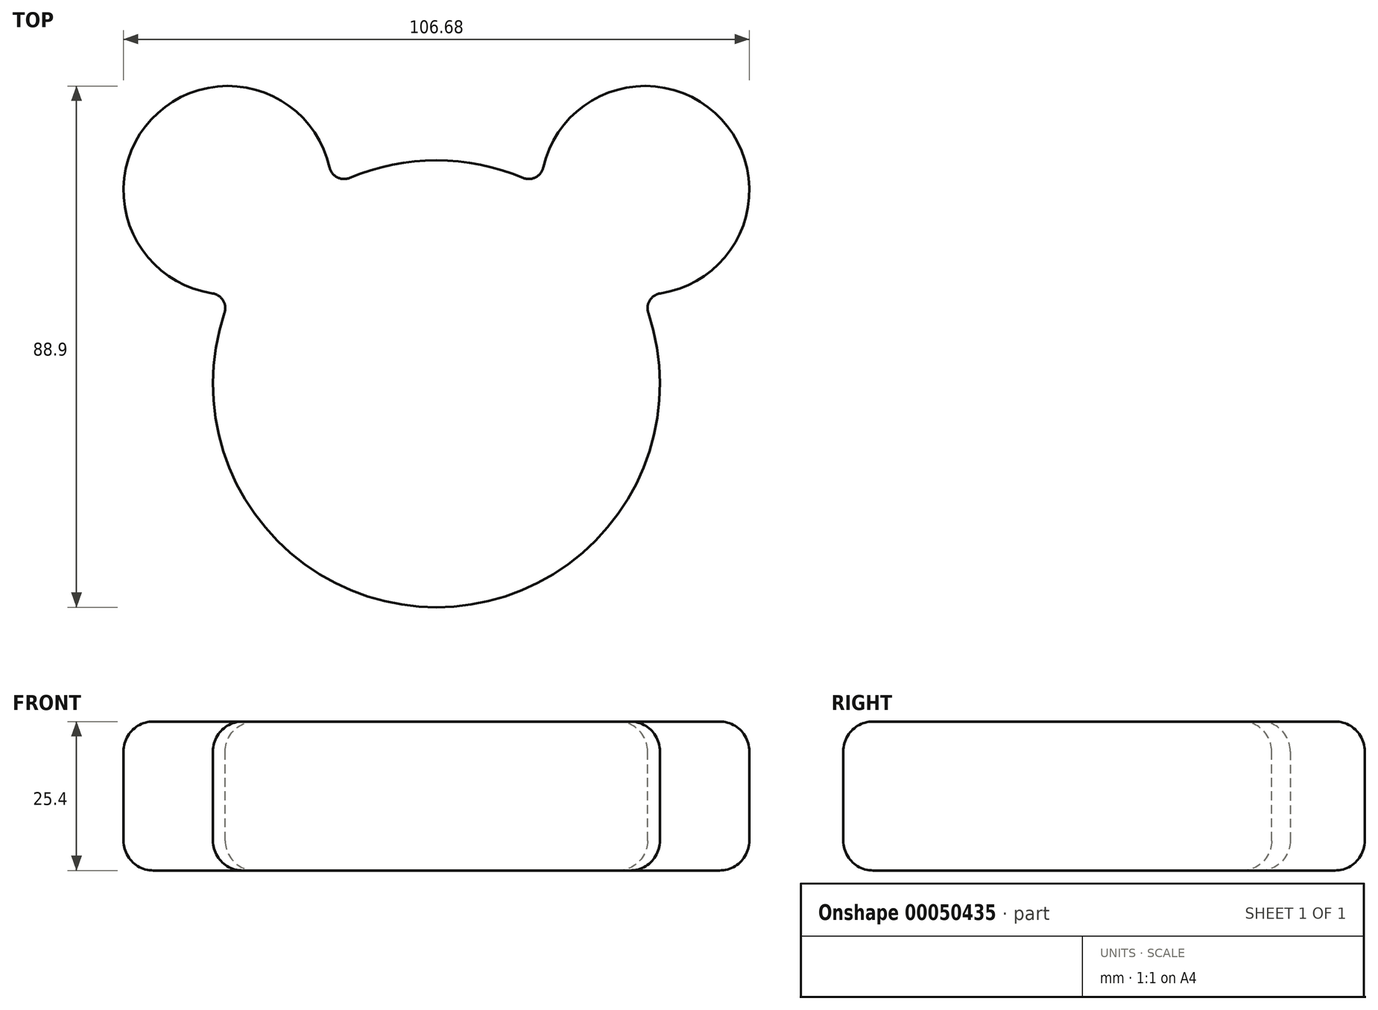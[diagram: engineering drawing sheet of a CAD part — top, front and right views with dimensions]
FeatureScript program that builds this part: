
annotation { "Feature Type Name" : "Feature", "Feature Type Description" : "" }
export const myFeature = defineFeature(function(context is Context, id is Id, definition is map)
    precondition{}
    {
        {
            var Q0;
            Q0=qCreatedBy(makeId("Top.planeOp"),FACE);
            var sketch = newSketch(context, id + "F0", { "sketchPlane" : qUnion([Q0])});
            skArc(sketch, "E0", {"start": v(-34.91, 15.25) * mm, "mid": v(0, -38.1) * mm, "end": v(34.91, 15.25) * mm});
            skArc(sketch, "E1", {"start": v(-17.8, 33.7) * mm, "mid": v(-48.59, 45.12) * mm, "end": v(-34.91, 15.25) * mm});
            skArc(sketch, "E2", {"start": v(34.91, 15.25) * mm, "mid": v(48.59, 45.12) * mm, "end": v(17.8, 33.7) * mm});
            skLineSegment(sketch, "E3", {"start": v(-35.56, 33.02) * mm, "end": v(0, 33.02) * mm, "construction": true});
            skLineSegment(sketch, "E4", {"start": v(0, 33.02) * mm, "end": v(35.56, 33.02) * mm, "construction": true});
            skArc(sketch, "E5.trimOffspring", {"start": v(17.8, 33.7) * mm, "mid": v(0, 38.1) * mm, "end": v(-17.8, 33.7) * mm});
            skSolve(sketch);
        }
        {
            var Q0;
            Q0=makeQuery(id+"F0.imprint","IMPRINT",FACE,{"disambiguationData":[TD([[makeQuery(id+"F0.imprint","IMPRINT",EDGE,{"derivedFrom":sQuery(id+"F0.wireOp",EDGE,"E0")}),1.0]])]});
            extrude(context, id + "F1", {"entities" : qUnion([Q0]), "depth" : 25.4 * mm});
        }
        {
            var Q0;
            Q0=makeQuery(id+"F1.opExtrude","SWEPT_EDGE",EDGE,{"disambiguationData":[OSD([sQuery(id+"F0.wireOp",EDGE,"E0"),sQuery(id+"F0.wireOp",EDGE,"E1")])]});
            var Q1;
            Q1=makeQuery(id+"F1.opExtrude","SWEPT_EDGE",EDGE,{"disambiguationData":[OSD([sQuery(id+"F0.wireOp",EDGE,"E1"),sQuery(id+"F0.wireOp",EDGE,"E5.trimOffspring")])]});
            var Q2;
            Q2=makeQuery(id+"F1.opExtrude","SWEPT_EDGE",EDGE,{"disambiguationData":[OSD([sQuery(id+"F0.wireOp",EDGE,"E2"),sQuery(id+"F0.wireOp",EDGE,"E5.trimOffspring")])]});
            var Q3;
            Q3=makeQuery(id+"F1.opExtrude","SWEPT_EDGE",EDGE,{"disambiguationData":[OSD([sQuery(id+"F0.wireOp",EDGE,"E0"),sQuery(id+"F0.wireOp",EDGE,"E2")])]});
            fillet(context, id + "F2", {"entities" : qUnion([Q0, Q1, Q2, Q3]), "radius" : 2.54 * mm, "tangentPropagation" : true, "allowEdgeOverflow" : false});
        }
        {
            var Q0;
            Q0=makeQuery(id+"F1.opExtrude","CAP_EDGE",EDGE,{"disambiguationData":[OSD([sQuery(id+"F0.wireOp",EDGE,"E0")])],"isStart":false});
            var Q1;
            Q1=makeQuery(id+"F1.opExtrude","CAP_EDGE",EDGE,{"disambiguationData":[OSD([sQuery(id+"F0.wireOp",EDGE,"E0")])],"isStart":true});
            fillet(context, id + "F3", {"entities" : qUnion([Q0, Q1]), "radius" : 5.08 * mm, "tangentPropagation" : true, "allowEdgeOverflow" : false});
        }
    });
